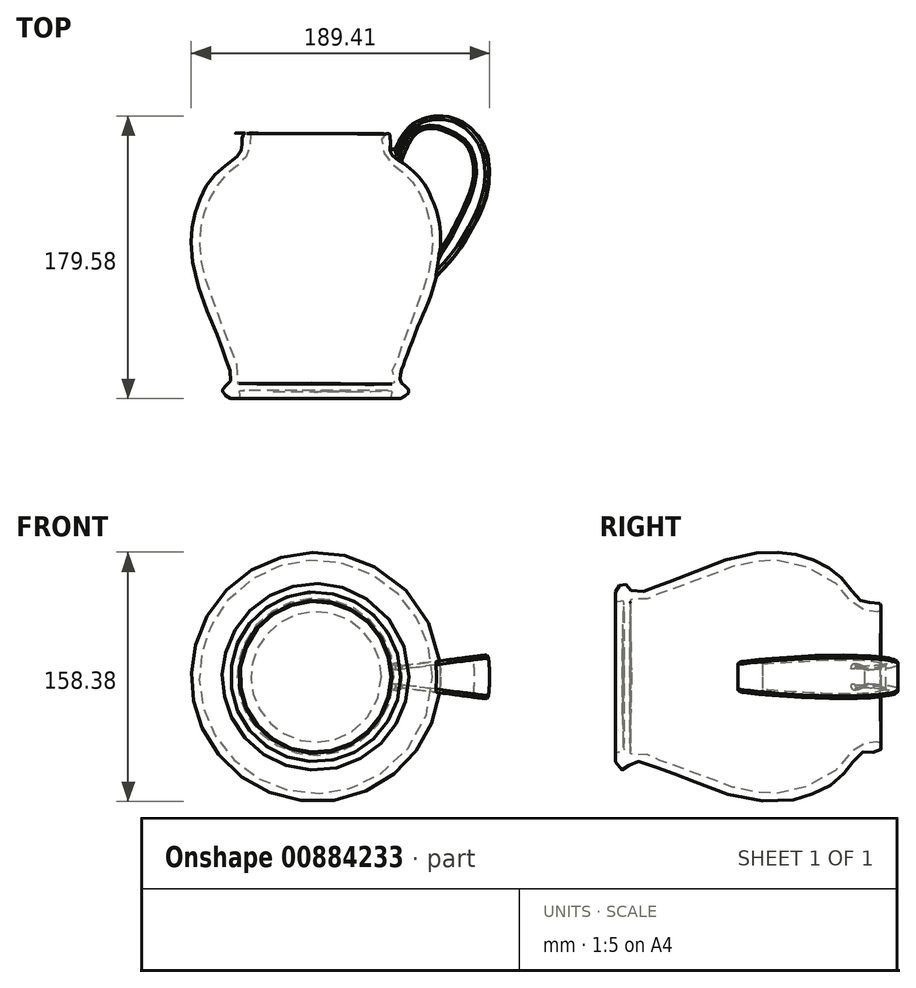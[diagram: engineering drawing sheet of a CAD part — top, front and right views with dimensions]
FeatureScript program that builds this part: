
annotation { "Feature Type Name" : "Feature", "Feature Type Description" : "" }
export const myFeature = defineFeature(function(context is Context, id is Id, definition is map)
    precondition{}
    {
        {
            var Q0;
            Q0=qCreatedBy(makeId("Top.planeOp"),FACE);
            var sketch = newSketch(context, id + "F0", { "sketchPlane" : qUnion([Q0])});
            skFitSpline(sketch, "E0", {"points": [v(149.3, -82.28) * mm, v(144.46, -76.94) * mm, v(144.46, -69.81) * mm, v(148.02, -59.9) * mm, v(154.89, -41.84) * mm, v(161, -27.34) * mm, v(166.59, -10.55) * mm, v(169.13, 5.47) * mm, v(168.62, 24.29) * mm, v(163.28, 41.07) * mm, v(155.4, 53.8) * mm, v(142.43, 64.73) * mm, v(137.85, 70.58) * mm, v(136.83, 80.83) * mm, v(134.54, 80.83) * mm, v(132.5, 80.83) * mm, v(132.25, 73.37) * mm, v(134.54, 66.76) * mm, v(139.63, 60.91) * mm, v(146.24, 55.83) * mm, v(153.36, 47.69) * mm, v(158.45, 38.28) * mm, v(162.27, 27.09) * mm, v(164.3, 15.39) * mm, v(163.54, 2.67) * mm, v(160.74, -11.32) * mm, v(155.4, -25.56) * mm, v(150.57, -39.04) * mm, v(145.23, -53.03) * mm, v(140.9, -64.73) * mm, v(138.61, -70.58) * mm, v(139.88, -77.44) * mm, v(137.85, -77.95) * mm, v(127.42, -78.2) * mm, v(112.92, -77.7) * mm, v(98.68, -77.44) * mm, v(89.27, -77.7) * mm, v(89.53, -79.22) * mm, v(89.53, -82.53) * mm, v(96.14, -82.53) * mm, v(110.9, -82.78) * mm, v(129.97, -82.53) * mm, v(138.36, -82.78) * mm, v(138.1, -84.57) * mm, v(138.36, -87.1) * mm, v(143.95, -87.36) * mm, v(149.3, -82.28) * mm]});
            skLineSegment(sketch, "E1", {"start": v(36.08, -87.1) * mm, "end": v(143.95, -87.36) * mm});
            skLineSegment(sketch, "E2", {"start": v(90.02, -89.83) * mm, "end": v(90.46, 90.8) * mm});
            skPoint(sketch, "E2.startSnap0", {"position": v(90.02, -87.23) * mm});
            skSolve(sketch);
        }
        {
            var Q0;
            Q0=qCreatedBy(makeId("Top.planeOp"),FACE);
            var sketch = newSketch(context, id + "F1", { "sketchPlane" : qUnion([Q0])});
            skFitSpline(sketch, "E3", {"points": [v(162.27, -14.37) * mm, v(175.74, 0) * mm, v(185.16, 12.84) * mm, v(195.07, 31.16) * mm, v(199.4, 44.64) * mm, v(199.9, 64.47) * mm, v(194.57, 77.7) * mm, v(187.7, 85.58) * mm, v(181.6, 89.4) * mm, v(176, 91.43) * mm, v(167.86, 92.2) * mm, v(159.47, 90.67) * mm, v(151.33, 86.6) * mm, v(145.23, 79.73) * mm, v(141.16, 71.6) * mm, v(138.87, 64.73) * mm, v(138.87, 64.98) * mm], "startDerivative": vector(166.04, 170.23) * mm, "endDerivative": vector(3.44, 39.55) * mm});
            skLineSegment(sketch, "E4", {"start": v(138.87, 64.98) * mm, "end": v(143.43, 60.68) * mm});
            skFitSpline(sketch, "E5", {"points": [v(143.43, 60.68) * mm, v(147.22, 70.08) * mm, v(151.92, 78.62) * mm, v(157.42, 83.1) * mm, v(165.54, 84.3) * mm, v(173.83, 81.89) * mm, v(183.74, 76.36) * mm, v(188.9, 69.1) * mm, v(190.9, 54.47) * mm, v(187.08, 40.07) * mm, v(179.57, 24.11) * mm, v(173.4, 12.6) * mm, v(166.02, 0) * mm, v(162.27, -14.37) * mm], "startDerivative": vector(50.18, 130.73) * mm, "endDerivative": vector(-30.89, -169.5) * mm});
            skSolve(sketch);
        }
        {
            var Q0;
            {var subQ0=sQuery(id+"F0.wireOp",EDGE,"E2");var subQ1=sQuery(id+"F0.wireOp",EDGE,"E0");var subQ2=makeQuery(id+"F0.imprint","INTERSECT",VERTEX,{"disambiguationData":[OD(1.0)],"derivedFrom":[subQ1,subQ0]});Q0=makeQuery(id+"F0.imprint","IMPRINT",FACE,{"disambiguationData":[TD([[makeQuery(id+"F0.imprint","IMPRINT",EDGE,{"disambiguationData":[TD([[subQ2,-1.0]])],"derivedFrom":subQ1}),1.0]])]});}
            var Q1;
            Q1=sQuery(id+"F0.wireOp",EDGE,"E0");
            var Q2;
            Q2=sQuery(id+"F0.wireOp",EDGE,"E2");
            revolve(context, id + "F2", {"surfaceOperationType" : NewSurfaceOperationType.ADD, "entities" : qUnion([Q0]), "surfaceEntities" : qUnion([Q1]), "axis" : qUnion([Q2]), "revolveType" : RevolveType.FULL});
        }
        {
            var Q0;
            {var subQ0=sQuery(id+"F1.wireOp",EDGE,"E5");Q0=makeQuery(id+"F1.imprint","IMPRINT",FACE,{"disambiguationData":[TD([[makeQuery(id+"F1.imprint","IMPRINT",EDGE,{"derivedFrom":subQ0}),1.0]])]});}
            var Q1;
            Q1=sQuery(id+"F1.wireOp",EDGE,"E3");
            var Q2;
            Q2=sQuery(id+"F1.wireOp",EDGE,"E5");
            var Q3;
            Q3=sQuery(id+"F1.wireOp",EDGE,"E4");
            var Q4;
            {var subQ0=sQuery(id+"F0.wireOp",EDGE,"E0");Q4=makeQuery(id+"F2.opRevolve","SWEPT_FACE",FACE,{"disambiguationData":[OSD([subQ0]),TDD([makeQuery(id+"F0.imprint","IMPRINT",EDGE,{"disambiguationData":[TD([[makeQuery(id+"F0.imprint","INTERSECT",VERTEX,{"disambiguationData":[OD(0.0)],"derivedFrom":[subQ0,sQuery(id+"F0.wireOp",EDGE,"E1")]}),-1.0]])],"derivedFrom":subQ0})])]});}
            revolve(context, id + "F3", {"operationType" : NewBodyOperationType.ADD, "surfaceOperationType" : NewSurfaceOperationType.NEW, "entities" : qUnion([Q0]), "surfaceEntities" : qUnion([Q1, Q2, Q3]), "axis" : qUnion([Q4]), "revolveType" : RevolveType.SYMMETRIC, "angle" : 14.66 * degree});
        }
        {
            var Q0;
            Q0=makeQuery(id+"F3.opRevolve","CAP_EDGE",EDGE,{"disambiguationData":[OSD([sQuery(id+"F1.wireOp",EDGE,"E5")])],"isStart":false});
            var Q1;
            Q1=makeQuery(id+"F3.opRevolve","CAP_EDGE",EDGE,{"disambiguationData":[OSD([sQuery(id+"F1.wireOp",EDGE,"E3")])],"isStart":false});
            var Q2;
            Q2=makeQuery(id+"F3.opRevolve","CAP_EDGE",EDGE,{"disambiguationData":[OSD([sQuery(id+"F1.wireOp",EDGE,"E5")])],"isStart":true});
            var Q3;
            Q3=makeQuery(id+"F3.opRevolve","CAP_EDGE",EDGE,{"disambiguationData":[OSD([sQuery(id+"F1.wireOp",EDGE,"E3")])],"isStart":true});
            fillet(context, id + "F4", {"entities" : qUnion([Q0, Q1, Q2, Q3]), "radius" : 2 * mm, "tangentPropagation" : true, "allowEdgeOverflow" : false});
        }
        {
            var Q0;
            {var subQ0=sQuery(id+"F0.wireOp",EDGE,"E0");Q0=makeQuery(id+"F3.boolean.opBoolean","INTERSECT",EDGE,{"disambiguationData":[OD(1.0)],"derivedFrom":[makeQuery(id+"F2.opRevolve","SWEPT_FACE",FACE,{"disambiguationData":[OSD([subQ0]),TDD([makeQuery(id+"F0.imprint","IMPRINT",EDGE,{"disambiguationData":[TD([[makeQuery(id+"F0.imprint","INTERSECT",VERTEX,{"disambiguationData":[OD(0.0)],"derivedFrom":[subQ0,sQuery(id+"F0.wireOp",EDGE,"E1")]}),-1.0]])],"derivedFrom":subQ0})])]}),makeQuery(id+"F3.opRevolve","SWEPT_FACE",FACE,{"disambiguationData":[OSD([sQuery(id+"F1.wireOp",EDGE,"E5")])]})]});}
            fillet(context, id + "F5", {"entities" : qUnion([Q0]), "radius" : 2 * mm, "tangentPropagation" : true, "allowEdgeOverflow" : false});
        }
    });
